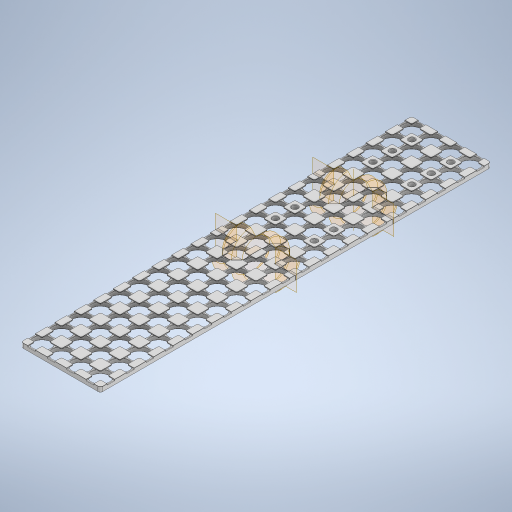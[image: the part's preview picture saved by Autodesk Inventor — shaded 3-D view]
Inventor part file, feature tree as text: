
AUTODESK INVENTOR PART (.ipt)
format: ipt  version: 2024.2 (Build 282272000, 272)  size: 6,368,256 bytes
history: native  units: mm
features: other x22, surface_op x13, chamfer x9, revolve x7, thicken_offset x6, pattern_linear x5, sketch x5, extrude x3, fillet x3, hole x2, split x2, pattern_circular x1
ambient origin geometry x8: Origin, YZ Plane, XZ Plane, XY Plane, X Axis, Y Axis, Z Axis, Center Point
bodies: Solid1 (feature_tree), Solid2 (feature_tree), Solid4 (feature_tree)
feature tree (78):
  extrude  "Extrusion1"  Depth=23.5mm
  extrude  "Extrusion2"  Depth=5.0mm TaperAngle=0.0deg
  fillet  "Fillet1"  Radius=7.25mm
  chamfer  "Chamfer1"  Distance=1.0mm
  chamfer  "Chamfer2"  Distance=0.4mm Angle=45.0deg
  pattern_linear  "Rectangular Pattern1"  Count1=4 Spacing1=23.5mm
  sketch  "Sketch3"  dims[d6=7.25mm d7=1.0mm d8=0.0mm]
  surface_op  "Stitch Surface1"
  other  "Work Axis1"
  pattern_circular  "Circular Pattern1"  Count=20  [1 undecoded]
  surface_op  "Extend3"
  surface_op  "Extend4"
  surface_op  "Stitch Surface8"
  pattern_linear  "Rectangular Pattern2"  Spacing1=23.5mm  [1 undecoded]
  hole  "Hole1"  [1 undecoded]
  chamfer  "Chamfer3"  Distance=23.5mm
  hole  "Hole2"  [1 undecoded]
  chamfer  "Chamfer4"  Distance=13.0mm
  pattern_linear  "Rectangular Pattern4"  Count1=2 Spacing1=23.5mm
  pattern_linear  "Rectangular Pattern5"  Spacing1=10.0mm  [1 undecoded]
  chamfer  "Chamfer5"  Distance=23.5mm
  chamfer  "Chamfer6"  Angle=180.0deg  [1 undecoded]
  thicken_offset  "Thicken8"
  fillet  "Fillet2"  [1 undecoded]
  chamfer  "Chamfer7"  Angle=180.0deg  [1 undecoded]
  chamfer  "Chamfer8"  Angle=180.0deg  [1 undecoded]
  chamfer  "Chamfer9"  Angle=90.0deg  [1 undecoded]
  split  "Split1"
  thicken_offset  "Thicken3"
  thicken_offset  "Thicken4"
  pattern_linear  "Rectangular Pattern6"  Spacing1=90.0deg  [1 undecoded]
  surface_op  "Stitch Surface11"
  split  "Split2"
  thicken_offset  "Thicken5"
  thicken_offset  "Thicken6"
  thicken_offset  "Thicken7"
  fillet  "Fillet3"  [1 undecoded]
  sketch  "Sketch1"  dims[d0=23.5mm d1=23.5mm]
  sketch  "Sketch2"  dims[d2=21.7mm d3=5.0mm d4=0.0mm d5=7.25mm]
  other  "Srf1"
  other  "Srf2"
  other  "Srf3"
  other  "Srf4"
  other  "Srf5"
  other  "Srf6"
  other  "Srf7"
  other  "Srf8"
  other  "Srf9"
  other  "Srf10"
  other  "Srf11"
  other  "Srf12"
  other  "Srf14"
  other  "Srf13"
  other  "Srf15"
  other  "Srf17"
  sketch  "Sketch4"  dims[d9=2.0mm d10=0.4mm d11=2.0mm d12=45.0deg]
  sketch  "Sketch5"  dims[d13=0.2mm d14=2.0mm d15=45.0deg d16=40.0mm d18=23.5mm d19=200.0mm d21=23.5mm d22=23.5mm d23=23.5mm d27=23.5mm d29=45.0deg d30=13.0mm d31=20.0mm d33=23.5mm d34=10.0mm d36=23.5mm d39=23.5mm d41=180.0deg d42=90.0deg d43=180.0deg d44=180.0deg d45=90.0deg d46=90.0deg d47=90.0deg d48=34.0mm d49=0.0mm d50=20.0mm d51=360.0deg d59=30.0mm d61=117.5mm d64=6.756mm d65=6.0mm d66=12.878mm d67=2.0mm d68=14.3117mm d69=8.0mm d70=0.0mm d71=0.5mm d72=2.0mm d73=45.0deg d80=6.756mm d81=6.0mm d82=4.0mm d83=2.0mm d84=90.0deg d85=8.0mm d86=0.0mm d87=0.5mm d88=2.0mm d89=45.0deg d90=20.0mm d92=47.0mm d93=20.0mm d95=23.5mm d96=30.0mm d98=23.5mm d99=20.0mm d101=47.0mm d102=0.5mm d103=2.0mm d104=45.0deg d105=0.5mm d106=2.0mm d107=45.0deg d108=0.3mm d109=0.3mm d110=0.3mm d111=0.3mm d112=20.0mm d114=117.5mm d115=0.3mm d116=0.3mm d117=0.3mm d118=0.3mm d119=0.3mm d120=0.3mm d121=1.0mm d122=1.0mm d123=2.0mm d124=2.0mm d125=0.5mm d126=2.0mm d127=45.0deg d128=0.2mm d129=2.0mm d130=45.0deg d131=0.5mm d132=2.0mm d133=45.0deg d134=3.0mm d135=1.25mm]
  other  "Srf18"
  other  "Srf19"
  other  "Srf20"
  revolve  "RevolutionSrf1"  [1 undecoded]
  revolve  "RevolutionSrf2"  [1 undecoded]
  revolve  "RevolutionSrf3"  Angle=360.0deg
  revolve  "RevolutionSrf4"  [1 undecoded]
  revolve  "RevolutionSrf5"  Angle=45.0deg
  revolve  "RevolutionSrf6"  Angle=45.0deg
  revolve  "RevolutionSrf7"  [1 undecoded]
  extrude  "ExtrusionSrf1"  Depth=23.5mm
  surface_op  "Stitch Surface2"
  surface_op  "Stitch Surface3"
  surface_op  "Stitch Surface4"
  surface_op  "Stitch Surface5"
  surface_op  "Stitch Surface6"
  other  "End"
  surface_op  "Stitch Surface9"
  surface_op  "Stitch Surface10"
  other  "Middle"
  surface_op  "Boundary Patch1"
note: 16 required parameter values undecoded (feature->parameter linkage not recoverable at this tier; creation-order binding heuristic only, values carry confidence <= 0.55)